# Revit family: Deca_Chuv. 1 - Aquamax_Chuveiro área externa _1998.EXT
name_source: partatom
category: Plumbing Fixtures
units: mm (PartAtom-declared; Revit-internal decimal feet)

## family parameters
Cut with Voids When Loaded = No
Host = Face
Part Type = Normal
Room Calculation Point = No
Round Connector Dimension = Use Radius
Shared = No

## types (2) — shared parameters
Acompanha o Produto = Base
Aprovado por = quattroD
Atendimento ao Cliente = 0800-0117073
Categoria = Chuveiro / Duchas
Composição Básica = Liga de Cobre (Latão),Plásticos de Engenharia, Aço Inoxidavel e Elastômeros
Consumo = -
Cor Secundária = -
Criado por = quattroD
Itens de Instalação = -
Linha = Chuveiro de Área Externa
Manufacturer = DECA
Norma = Não possui
Pressão mín. Aquec. Acúmulo = -
Pressão mín. Aquec. Passagem = -
Saída de Esgoto = -
Segmento = Luxo
Tipo de dispositivo economizador = -
Tipo de mecanismo utilizado = Mecanismo 1/2 volta com desviador
Tipo de rosca de entrada = BSP
Tipo de rosca de saída = -
URL = www.deca.com.br
zero-valued in all types: CWFU, Default Elevation, Diâmetro Ponto de Esgoto, Diâmetro Água Fria, Peso Líquido (Kg), Raio Ponto de Esgoto, Raio Água Fria, WFU

## per-type parameters (varying)
| type | Cor Principal | Código Pai | Material | Model |
| 1998.C.EXT_Cromado | Cromado | 1998.C.EXT | Deca_Cromado | 1998.C.EXT |
| 1998.BL.EXT.MT | Black Matte | 1998.BL.EXT.MT | Deca_Black Matte | 1998.BL.EXT.MT |

## geometry (parser evidence)
native form markers: Sweep x1
no freeform markers — native parametric forms only
